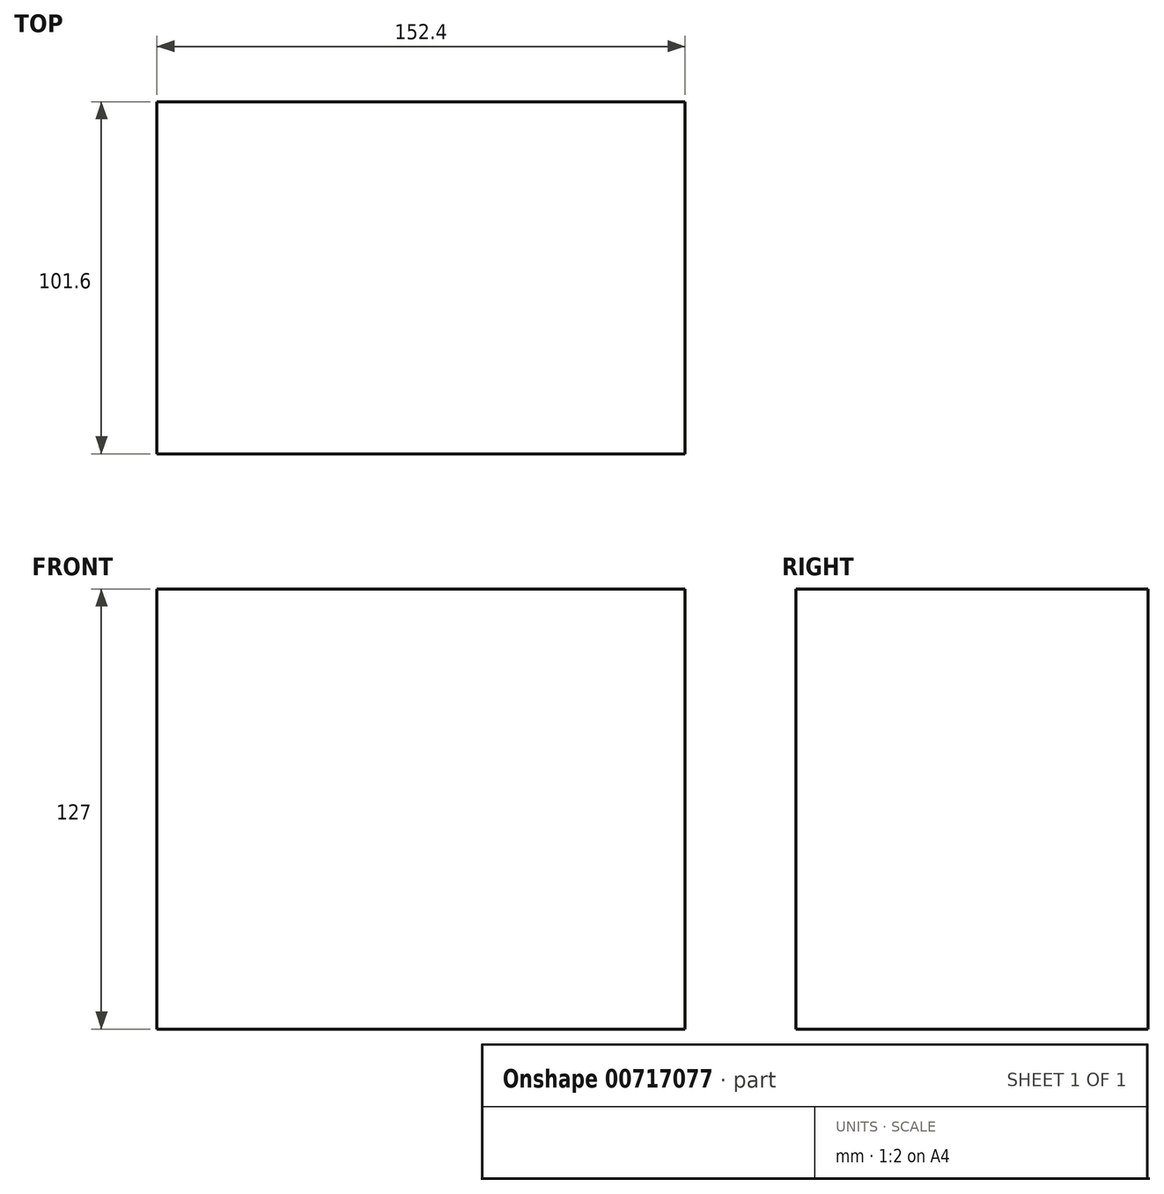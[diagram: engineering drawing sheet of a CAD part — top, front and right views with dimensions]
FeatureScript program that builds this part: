
annotation { "Feature Type Name" : "Feature", "Feature Type Description" : "" }
export const myFeature = defineFeature(function(context is Context, id is Id, definition is map)
    precondition{}
    {
        {
            var Q0;
            Q0=qCreatedBy(makeId("Front.planeOp"),FACE);
            var sketch = newSketch(context, id + "F0", { "sketchPlane" : qUnion([Q0])});
            skLineSegment(sketch, "E0", {"start": v(-69.64, -71.98) * mm, "end": v(82.76, -71.98) * mm});
            skLineSegment(sketch, "E1", {"start": v(82.76, -71.98) * mm, "end": v(82.76, 55.02) * mm});
            skLineSegment(sketch, "E2", {"start": v(-69.64, -71.98) * mm, "end": v(-69.64, 55.02) * mm});
            skLineSegment(sketch, "E3", {"start": v(-69.64, 55.02) * mm, "end": v(82.76, 55.02) * mm});
            skLineSegment(sketch, "E4", {"start": v(82.76, 55.02) * mm, "end": v(156.3, 124.62) * mm});
            skSolve(sketch);
        }
        {
            var Q0;
            Q0 = qSketchRegion(id + "F0", true);
            extrude(context, id + "F1", {"entities" : qUnion([Q0]), "depth" : 101.6 * mm, "offsetDistance" : 25.4 * mm});
        }
    });
